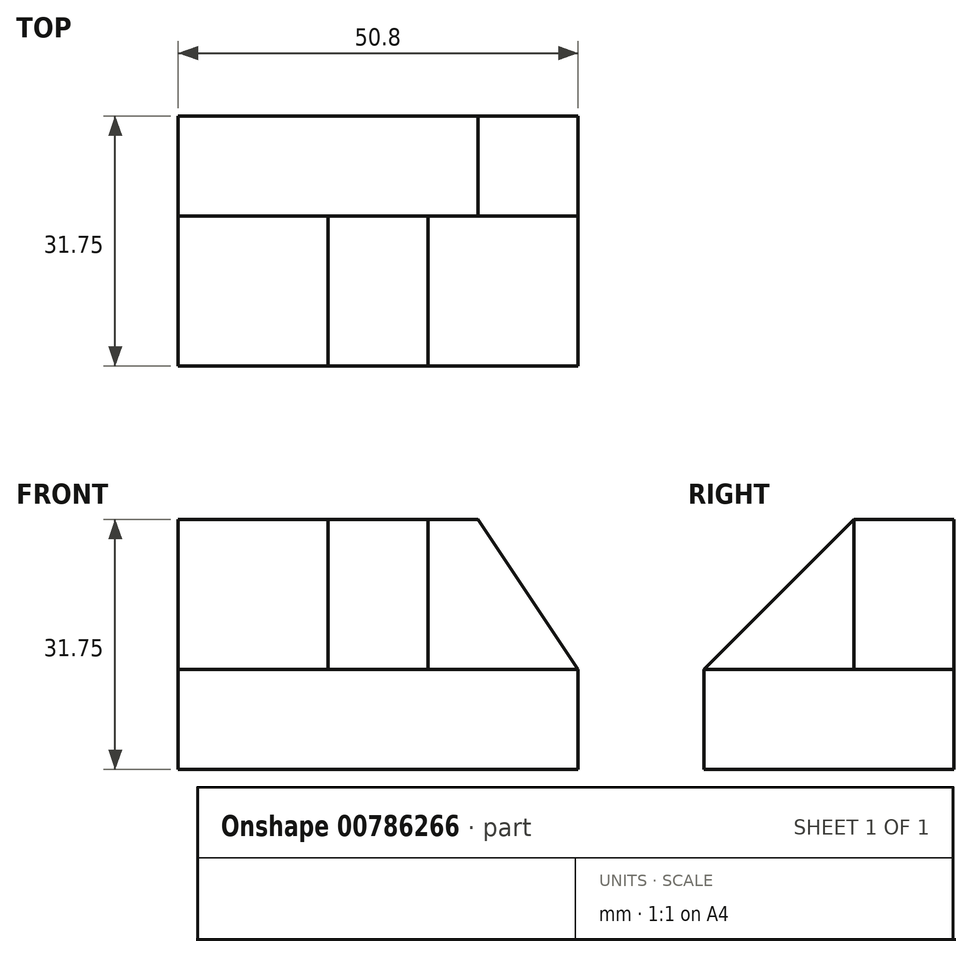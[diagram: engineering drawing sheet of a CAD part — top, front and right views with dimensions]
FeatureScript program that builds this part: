
annotation { "Feature Type Name" : "Feature", "Feature Type Description" : "" }
export const myFeature = defineFeature(function(context is Context, id is Id, definition is map)
    precondition{}
    {
        {
            var Q0;
            Q0=qCreatedBy(makeId("Front.planeOp"),FACE);
            var sketch = newSketch(context, id + "F0", { "sketchPlane" : qUnion([Q0])});
            skLineSegment(sketch, "E0", {"start": v(0, 0) * mm, "end": v(50.8, 0) * mm});
            skLineSegment(sketch, "E1", {"start": v(50.8, 0) * mm, "end": v(50.8, 31.75) * mm});
            skLineSegment(sketch, "E2", {"start": v(50.8, 31.75) * mm, "end": v(0, 31.75) * mm});
            skLineSegment(sketch, "E3", {"start": v(0, 31.75) * mm, "end": v(0, 0) * mm});
            skSolve(sketch);
        }
        {
            var Q0;
            Q0 = qSketchRegion(id + "F0", true);
            extrude(context, id + "F1", {"entities" : qUnion([Q0]), "depth" : 31.75 * mm, "offsetDistance" : 25.4 * mm});
        }
        {
            var Q0;
            Q0=makeQuery(id+"F1.opExtrude","SWEPT_FACE",FACE,{"disambiguationData":[OSD([sQuery(id+"F0.wireOp",EDGE,"E1")])]});
            var sketch = newSketch(context, id + "F2", { "sketchPlane" : qUnion([Q0])});
            skLineSegment(sketch, "E4", {"start": v(-31.75, 0) * mm, "end": v(-31.75, 12.7) * mm});
            skLineSegment(sketch, "E5", {"start": v(-31.75, 12.7) * mm, "end": v(-12.7, 12.7) * mm});
            skLineSegment(sketch, "E6", {"start": v(-12.7, 12.7) * mm, "end": v(-12.7, 31.75) * mm});
            skSolve(sketch);
        }
        {
            var Q0;
            {var subQ0=sQuery(id+"F2.wireOp",EDGE,"E5");Q0=makeQuery(id+"F2.imprint","IMPRINT",FACE,{"disambiguationData":[TD([[makeQuery(id+"F2.imprint","IMPRINT",EDGE,{"derivedFrom":subQ0}),1.0]])]});}
            extrude(context, id + "F3", {"entities" : qUnion([Q0]), "operationType" : NewBodyOperationType.REMOVE, "oppositeDirection" : true, "depth" : 19.05 * mm, "offsetDistance" : 25.4 * mm});
        }
        {
            var Q0;
            Q0=makeQuery(id+"F1.opExtrude","SWEPT_FACE",FACE,{"disambiguationData":[OSD([sQuery(id+"F0.wireOp",EDGE,"E3")])]});
            var sketch = newSketch(context, id + "F4", { "sketchPlane" : qUnion([Q0])});
            skLineSegment(sketch, "E7", {"start": v(31.75, 0) * mm, "end": v(31.75, 12.7) * mm});
            skLineSegment(sketch, "E8", {"start": v(31.75, 12.7) * mm, "end": v(12.7, 12.7) * mm});
            skLineSegment(sketch, "E9", {"start": v(12.7, 12.7) * mm, "end": v(12.7, 31.75) * mm});
            skSolve(sketch);
        }
        {
            var Q0;
            {var subQ0=sQuery(id+"F4.wireOp",EDGE,"E8");Q0=makeQuery(id+"F4.imprint","IMPRINT",FACE,{"disambiguationData":[TD([[makeQuery(id+"F4.imprint","IMPRINT",EDGE,{"derivedFrom":subQ0}),-1.0]])]});}
            extrude(context, id + "F5", {"entities" : qUnion([Q0]), "operationType" : NewBodyOperationType.REMOVE, "oppositeDirection" : true, "depth" : 19.05 * mm, "offsetDistance" : 25.4 * mm});
        }
        {
            var Q0;
            Q0=makeQuery(id+"F3.boolean.opBoolean","COPY",FACE,{"derivedFrom":makeQuery(id+"F3.opExtrude","CAP_FACE",FACE,{"disambiguationData":[OSD([sQuery(id+"F0.wireOp",EDGE,"E1"),sQuery(id+"F0.wireOp",EDGE,"E2"),sQuery(id+"F2.wireOp",EDGE,"E5"),sQuery(id+"F2.wireOp",EDGE,"E6")])],"isStart":false})});
            var sketch = newSketch(context, id + "F6", { "sketchPlane" : qUnion([Q0])});
            skLineSegment(sketch, "E10", {"start": v(-12.7, 31.75) * mm, "end": v(-31.75, 12.7) * mm});
            skSolve(sketch);
        }
        {
            var Q0;
            Q0=makeQuery(id+"F6.imprint","IMPRINT",FACE,{"disambiguationData":[TD([[makeQuery(id+"F6.imprint","IMPRINT",EDGE,{"derivedFrom":sQuery(id+"F6.wireOp",EDGE,"E10")}),-1.0]])]});
            extrude(context, id + "F7", {"entities" : qUnion([Q0]), "operationType" : NewBodyOperationType.REMOVE, "oppositeDirection" : true, "depth" : 12.7 * mm, "offsetDistance" : 25.4 * mm});
        }
        {
            var Q0;
            Q0=makeQuery(id+"F3.boolean.opBoolean","COPY",FACE,{"derivedFrom":makeQuery(id+"F3.opExtrude","SWEPT_FACE",FACE,{"disambiguationData":[OSD([sQuery(id+"F2.wireOp",EDGE,"E6")])]})});
            var sketch = newSketch(context, id + "F8", { "sketchPlane" : qUnion([Q0])});
            skLineSegment(sketch, "E11", {"start": v(31.75, 31.75) * mm, "end": v(38.1, 31.75) * mm});
            skLineSegment(sketch, "E12", {"start": v(38.1, 31.75) * mm, "end": v(50.8, 12.7) * mm});
            skSolve(sketch);
        }
        {
            var Q0;
            {var subQ0=sQuery(id+"F8.wireOp",EDGE,"E12");Q0=makeQuery(id+"F8.imprint","IMPRINT",FACE,{"disambiguationData":[TD([[makeQuery(id+"F8.imprint","IMPRINT",EDGE,{"derivedFrom":subQ0}),1.0]])]});}
            extrude(context, id + "F9", {"entities" : qUnion([Q0]), "operationType" : NewBodyOperationType.REMOVE, "oppositeDirection" : true, "depth" : 12.7 * mm, "offsetDistance" : 25.4 * mm});
        }
    });
